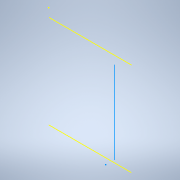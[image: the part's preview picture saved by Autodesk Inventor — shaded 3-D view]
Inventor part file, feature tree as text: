
AUTODESK INVENTOR PART (.ipt)
format: ipt  version: 2022 (Build 260153000, 153)  size: 84,480 bytes
history: native  units: mm
features: other x3, reference x2, sketch x1
ambient origin geometry x8: Origin, YZ Plane, XZ Plane, XY Plane, X Axis, Y Axis, Z Axis, Center Point
feature tree (6):
  sketch  "Sketch1"
  reference  "Reference1"
  reference  "Reference2"
  other  "Caja_Reductora_.iam"
  other  "Carcasa_CajaR_Lateral1:1"
  other  "Carcasa_CajaR_Lateral1:2"
